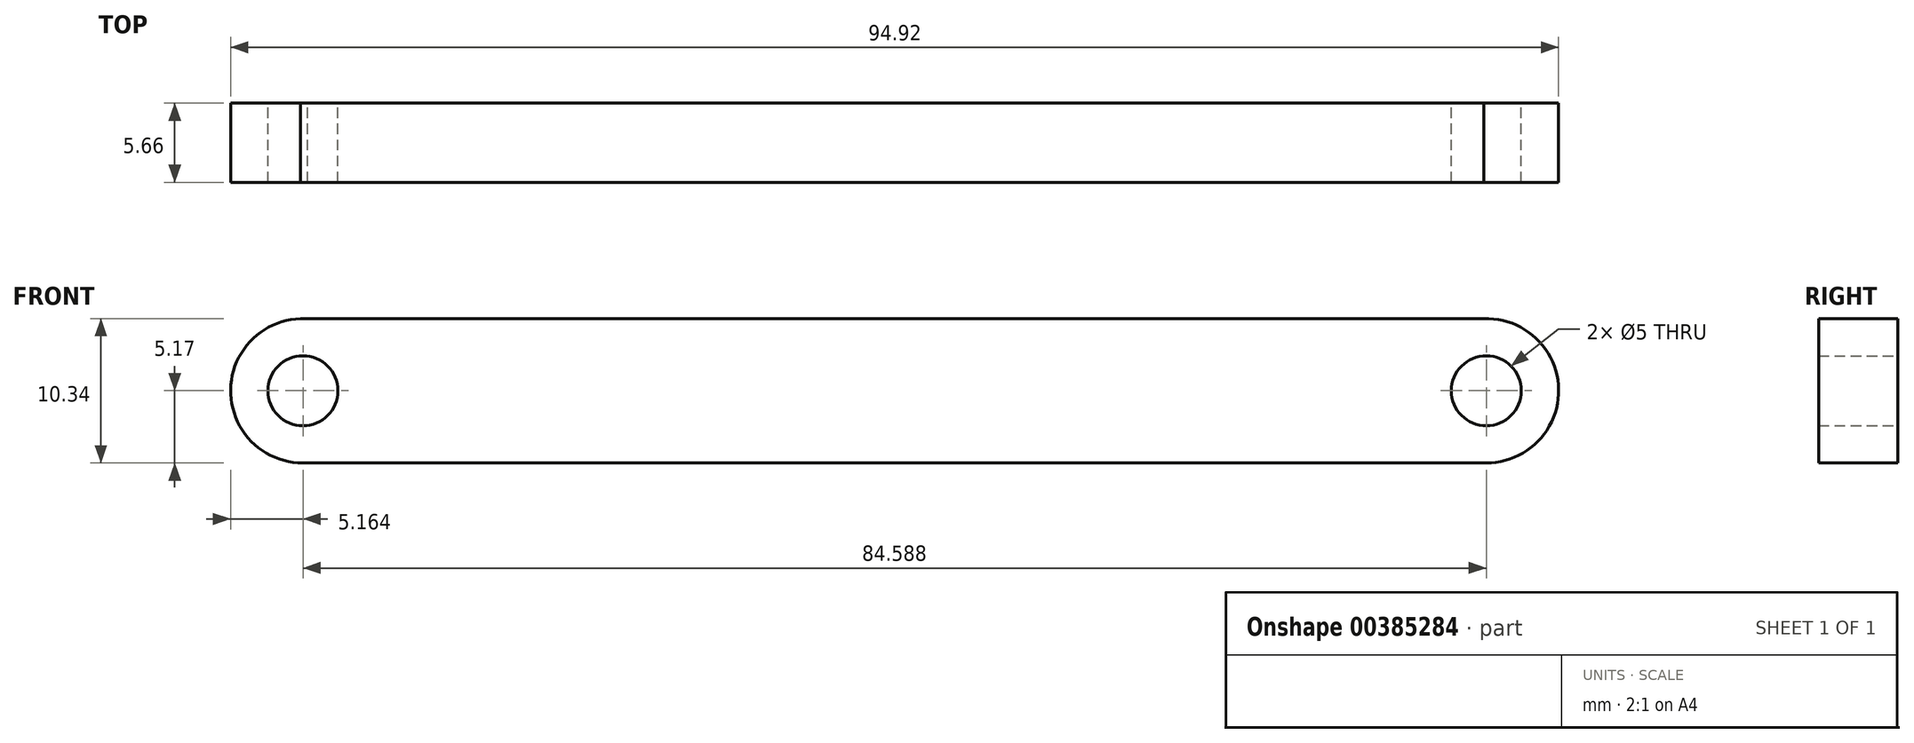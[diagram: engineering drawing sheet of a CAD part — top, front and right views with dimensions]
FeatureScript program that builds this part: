
annotation { "Feature Type Name" : "Feature", "Feature Type Description" : "" }
export const myFeature = defineFeature(function(context is Context, id is Id, definition is map)
    precondition{}
    {
        {
            var Q0;
            Q0=qCreatedBy(makeId("Front.planeOp"),FACE);
            var sketch = newSketch(context, id + "F0", { "sketchPlane" : qUnion([Q0])});
            skCircle(sketch, "E0", {"center": v(-22.2, 0) * mm, "radius": 2.5 * mm});
            skCircle(sketch, "E1", {"center": v(62.38, 0) * mm, "radius": 2.5 * mm});
            skArc(sketch, "E2", {"start": v(-22.03, 5.16) * mm, "mid": v(-27.37, -0.07) * mm, "end": v(-21.88, -5.16) * mm});
            skArc(sketch, "E3", {"start": v(62.38, -5.17) * mm, "mid": v(67.55, 0.09) * mm, "end": v(62.2, 5.16) * mm});
            skLineSegment(sketch, "E4", {"start": v(-22.38, 5.16) * mm, "end": v(62.2, 5.16) * mm});
            skLineSegment(sketch, "E5", {"start": v(-21.88, -5.16) * mm, "end": v(62.38, -5.17) * mm});
            skSolve(sketch);
        }
        {
            var Q0;
            Q0=makeQuery(id+"F0.imprint","IMPRINT",FACE,{"disambiguationData":[TD([[makeQuery(id+"F0.imprint","IMPRINT",EDGE,{"derivedFrom":sQuery(id+"F0.wireOp",EDGE,"E0")}),-1.0]])]});
            extrude(context, id + "F1", {"entities" : qUnion([Q0]), "depth" : 5.66 * mm});
        }
    });
